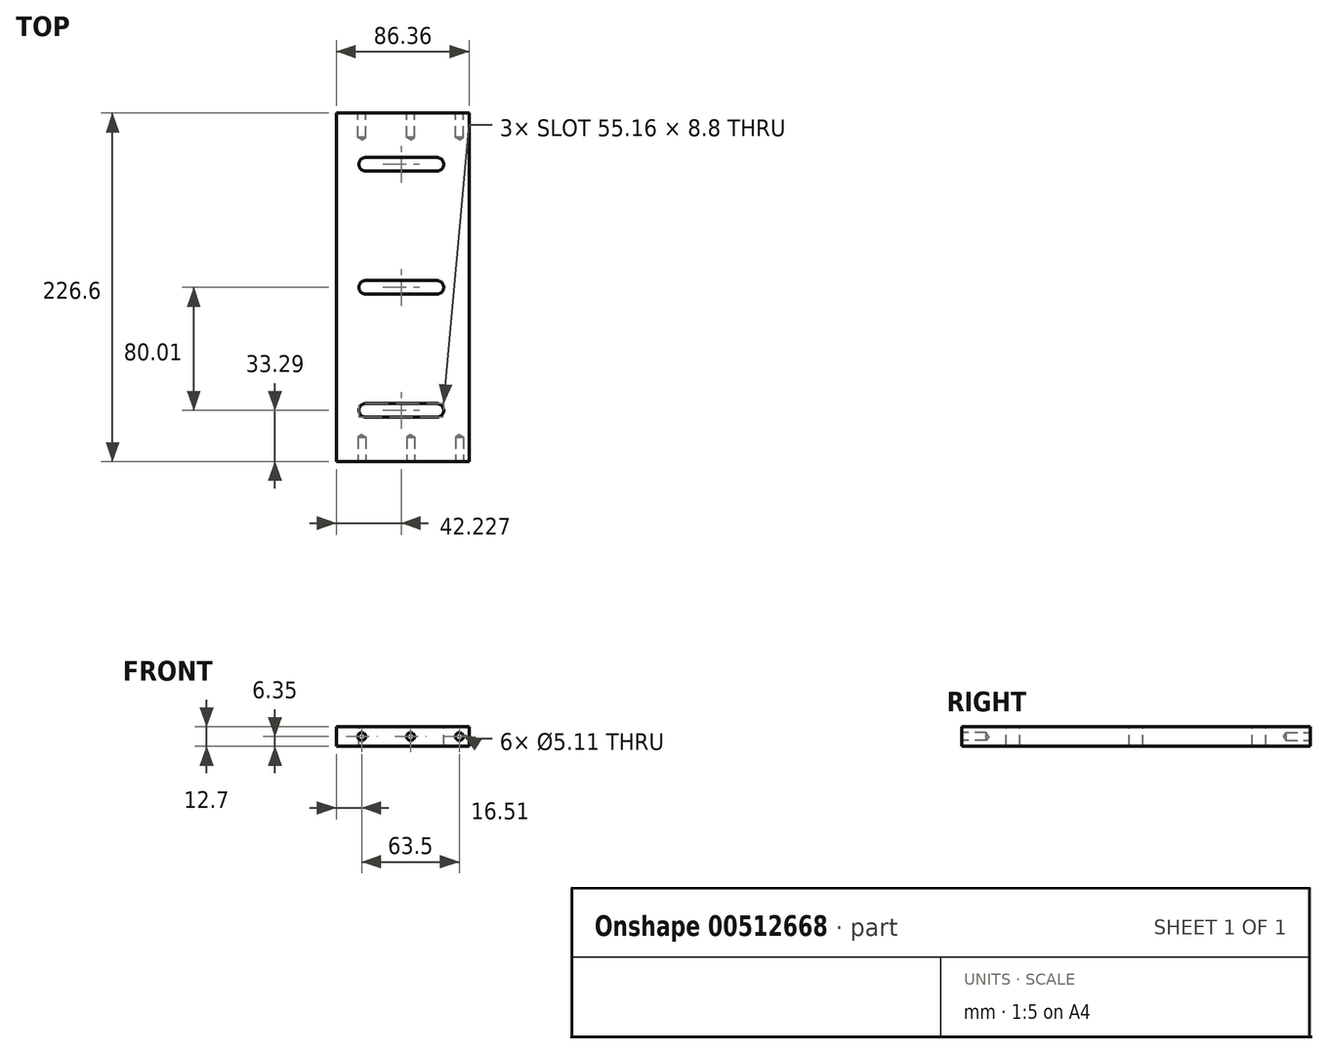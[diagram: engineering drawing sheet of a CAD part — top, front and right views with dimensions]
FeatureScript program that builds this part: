
annotation { "Feature Type Name" : "Feature", "Feature Type Description" : "" }
export const myFeature = defineFeature(function(context is Context, id is Id, definition is map)
    precondition{}
    {
        {
            var Q0;
            Q0=qCreatedBy(makeId("Front.planeOp"),FACE);
            var sketch = newSketch(context, id + "F0", { "sketchPlane" : qUnion([Q0])});
            skLineSegment(sketch, "E0.bottom", {"start": v(0, 0) * mm, "end": v(86.36, 0) * mm});
            skLineSegment(sketch, "E0.top", {"start": v(0, 12.7) * mm, "end": v(86.36, 12.7) * mm});
            skLineSegment(sketch, "E0.left", {"start": v(0, 0) * mm, "end": v(0, 12.7) * mm});
            skLineSegment(sketch, "E0.right", {"start": v(86.36, 0) * mm, "end": v(86.36, 12.7) * mm});
            skSolve(sketch);
        }
        {
            var Q0;
            Q0=makeQuery(id+"F0.imprint","IMPRINT",FACE,{"disambiguationData":[TD([[makeQuery(id+"F0.imprint","IMPRINT",EDGE,{"derivedFrom":sQuery(id+"F0.wireOp",EDGE,"E0.bottom")}),1.0]])]});
            extrude(context, id + "F1", {"entities" : qUnion([Q0]), "depth" : 252 * mm - 25.4 * mm, "offsetDistance" : 25.4 * mm});
        }
        {
            var Q0;
            Q0=makeQuery(id+"F1.opExtrude","SWEPT_FACE",FACE,{"disambiguationData":[OSD([sQuery(id+"F0.wireOp",EDGE,"E0.top")])]});
            var sketch = newSketch(context, id + "F2", { "sketchPlane" : qUnion([Q0])});
            skLineSegment(sketch, "E1", {"start": v(86.36, -226.6) * mm, "end": v(65.4, -226.6) * mm});
            skLineSegment(sketch, "E2", {"start": v(65.4, -226.6) * mm, "end": v(65.4, -193.3) * mm});
            skLineSegment(sketch, "E3", {"start": v(65.4, -193.3) * mm, "end": v(19.05, -193.3) * mm});
            skLineSegment(sketch, "E4", {"start": v(19.05, -193.3) * mm, "end": v(19.05, -113.3) * mm});
            skLineSegment(sketch, "E5", {"start": v(19.05, -113.3) * mm, "end": v(19.05, -33.29) * mm});
            skLineSegment(sketch, "E6", {"start": v(65.4, -193.3) * mm, "end": v(65.4, -113.3) * mm});
            skLineSegment(sketch, "E7", {"start": v(65.4, -113.3) * mm, "end": v(65.4, -33.29) * mm});
            skSolve(sketch);
        }
        {
            var Q0;
            Q0=sQuery(id+"F2.wireOp",VERTEX,"E5.start");
            var Q1;
            Q1=sQuery(id+"F2.wireOp",VERTEX,"E6.end");
            var Q2;
            Q2=sQuery(id+"F2.wireOp",VERTEX,"DjWuuTqk-Qcb5-qL21-kK1e-A5GOo4Qyxlcg.start");
            var Q3;
            Q3=sQuery(id+"F2.wireOp",VERTEX,"E7.end");
            var Q4;
            Q4=sQuery(id+"F2.wireOp",VERTEX,"uvlhDiYd-abZE-kXl5-hYny-CMJsfbRoTuFV.start");
            var Q5;
            Q5=sQuery(id+"F2.wireOp",VERTEX,"E4.start");
            var Q6;
            Q6=sQuery(id+"F2.wireOp",VERTEX,"E3.start");
            var Q7;
            Q7=sQuery(id+"F2.wireOp",VERTEX,"DjWuuTqk-Qcb5-qL21-kK1e-A5GOo4Qyxlcg.end");
            var Q8;
            Q8=sQuery(id+"F2.wireOp",VERTEX,"mJ9XW48N-7K4X-K1tE-wf8s-NppW8MMETJwE.end");
            var Q9;
            Q9=sQuery(id+"F2.wireOp",VERTEX,"E5.end");
            var Q10;
            Q10=makeQuery(id+"F1.opExtrude","SWEPT_BODY",BODY,{"disambiguationData":[OSD([sQuery(id+"F0.wireOp",EDGE,"E0.bottom"),sQuery(id+"F0.wireOp",EDGE,"E0.top"),sQuery(id+"F0.wireOp",EDGE,"E0.left"),sQuery(id+"F0.wireOp",EDGE,"E0.right")])]});
            hole(context, id + "F3", {"style" : HoleStyle.SIMPLE, "endStyle" : HoleEndStyle.THROUGH, "standardTappedOrClearance" : lookupTablePath({ "standard" : "ISO", "fit" : "Normal", "size" : "M8", "type" : "Clearance" }), "standardBlindInLast" : lookupTablePath({ "fit" : "Standard", "standard" : "ISO", "size" : "M8", "type" : "Clearance" }), "holeDiameter" : 8.8 * mm, "isTappedThrough" : true, "tappedDepth" : 12.7 * mm, "tapClearance" : 3, "locations" : qUnion([Q0, Q1, Q2, Q3, Q4, Q5, Q6, Q7, Q8, Q9]), "scope" : qUnion([Q10])});
        }
        {
            var Q0;
            Q0=makeQuery(id+"F1.opExtrude","SWEPT_FACE",FACE,{"disambiguationData":[OSD([sQuery(id+"F0.wireOp",EDGE,"E0.top")])]});
            var sketch = newSketch(context, id + "F4", { "sketchPlane" : qUnion([Q0])});
            skLineSegment(sketch, "E8", {"start": v(19.05, -193.3) * mm, "end": v(19.05, -197.7) * mm});
            skLineSegment(sketch, "E9", {"start": v(19.05, -197.7) * mm, "end": v(65.4, -197.7) * mm});
            skLineSegment(sketch, "E10", {"start": v(65.4, -197.7) * mm, "end": v(65.4, -188.9) * mm});
            skLineSegment(sketch, "E11", {"start": v(65.4, -188.9) * mm, "end": v(19.05, -188.9) * mm});
            skLineSegment(sketch, "E12", {"start": v(19.05, -188.9) * mm, "end": v(19.05, -193.3) * mm});
            skLineSegment(sketch, "E13.0.1.0", {"start": v(65.4, -108.9) * mm, "end": v(19.05, -108.9) * mm});
            skLineSegment(sketch, "E13.0.1.1", {"start": v(65.4, -117.7) * mm, "end": v(65.4, -108.9) * mm});
            skLineSegment(sketch, "E13.0.1.2", {"start": v(19.05, -117.7) * mm, "end": v(65.4, -117.7) * mm});
            skLineSegment(sketch, "E13.0.1.3", {"start": v(19.05, -108.9) * mm, "end": v(19.05, -113.3) * mm});
            skLineSegment(sketch, "E13.0.1.4", {"start": v(19.05, -113.3) * mm, "end": v(19.05, -117.7) * mm});
            skLineSegment(sketch, "E13.0.2.0", {"start": v(65.4, -28.89) * mm, "end": v(19.05, -28.89) * mm});
            skLineSegment(sketch, "E13.0.2.1", {"start": v(65.4, -37.69) * mm, "end": v(65.4, -28.89) * mm});
            skLineSegment(sketch, "E13.0.2.2", {"start": v(19.05, -37.69) * mm, "end": v(65.4, -37.69) * mm});
            skLineSegment(sketch, "E13.0.2.3", {"start": v(19.05, -28.89) * mm, "end": v(19.05, -33.29) * mm});
            skLineSegment(sketch, "E13.0.2.4", {"start": v(19.05, -33.29) * mm, "end": v(19.05, -37.69) * mm});
            skLineSegment(sketch, "E13.direction1", {"start": v(19.05, -197.7) * mm, "end": v(44.45, -197.7) * mm, "construction": true});
            skLineSegment(sketch, "E13.direction2", {"start": v(19.05, -197.7) * mm, "end": v(19.05, -117.7) * mm, "construction": true});
            skSolve(sketch);
        }
        {
            var Q0;
            Q0=makeQuery(id+"F1.opExtrude","CAP_FACE",FACE,{"disambiguationData":[OSD([sQuery(id+"F0.wireOp",EDGE,"E0.bottom"),sQuery(id+"F0.wireOp",EDGE,"E0.top"),sQuery(id+"F0.wireOp",EDGE,"E0.left"),sQuery(id+"F0.wireOp",EDGE,"E0.right")])],"isStart":false});
            var sketch = newSketch(context, id + "F5", { "sketchPlane" : qUnion([Q0])});
            skLineSegment(sketch, "E14", {"start": v(86.36, 6.35) * mm, "end": v(80.01, 6.35) * mm});
            skPoint(sketch, "E14.endSnap0", {"position": v(86.36, 6.35) * mm});
            skLineSegment(sketch, "E15", {"start": v(80.01, 6.35) * mm, "end": v(48.26, 6.35) * mm});
            skLineSegment(sketch, "E16", {"start": v(48.26, 6.35) * mm, "end": v(16.51, 6.35) * mm});
            skSolve(sketch);
        }
        {
            var Q0;
            Q0=sQuery(id+"F5.wireOp",VERTEX,"E16.end");
            var Q1;
            Q1=sQuery(id+"F5.wireOp",VERTEX,"E16.start");
            var Q2;
            Q2=sQuery(id+"F5.wireOp",VERTEX,"E15.start");
            var Q3;
            Q3=makeQuery(id+"F1.opExtrude","SWEPT_BODY",BODY,{"disambiguationData":[OSD([sQuery(id+"F0.wireOp",EDGE,"E0.bottom"),sQuery(id+"F0.wireOp",EDGE,"E0.top"),sQuery(id+"F0.wireOp",EDGE,"E0.left"),sQuery(id+"F0.wireOp",EDGE,"E0.right")])]});
            hole(context, id + "F6", {"style" : HoleStyle.SIMPLE, "endStyle" : HoleEndStyle.BLIND, "standardTappedOrClearance" : lookupTablePath({ "standard" : "ANSI", "engagement" : "75%", "pitch" : "20 tpi", "size" : "1/4", "type" : "Tapped" }), "standardBlindInLast" : lookupTablePath({ "standard" : "ANSI", "engagement" : "75%", "pitch" : "20 tpi", "size" : "1/4", "type" : "Tapped" }), "holeDiameter" : 5.1 * mm, "showTappedDepth" : true, "holeDepth" : 15.88 * mm, "isTappedThrough" : true, "tappedDepth" : 12.06 * mm, "tapClearance" : 3, "locations" : qUnion([Q0, Q1, Q2]), "scope" : qUnion([Q3]), "majorDiameter" : 6.35 * mm});
        }
        {
            var Q0;
            Q0=makeQuery(id+"F1.opExtrude","CAP_FACE",FACE,{"disambiguationData":[OSD([sQuery(id+"F0.wireOp",EDGE,"E0.bottom"),sQuery(id+"F0.wireOp",EDGE,"E0.top"),sQuery(id+"F0.wireOp",EDGE,"E0.left"),sQuery(id+"F0.wireOp",EDGE,"E0.right")])],"isStart":true});
            var sketch = newSketch(context, id + "F7", { "sketchPlane" : qUnion([Q0])});
            skLineSegment(sketch, "E17", {"start": v(-86.36, 6.35) * mm, "end": v(-80.01, 6.35) * mm});
            skLineSegment(sketch, "E18", {"start": v(-80.01, 6.35) * mm, "end": v(-48.26, 6.35) * mm});
            skLineSegment(sketch, "E19", {"start": v(-48.26, 6.35) * mm, "end": v(-16.51, 6.35) * mm});
            skSolve(sketch);
        }
        {
            var Q0;
            Q0=sQuery(id+"F7.wireOp",VERTEX,"E18.start");
            var Q1;
            Q1=sQuery(id+"F7.wireOp",VERTEX,"E19.start");
            var Q2;
            Q2=sQuery(id+"F7.wireOp",VERTEX,"E19.end");
            var Q3;
            Q3=makeQuery(id+"F1.opExtrude","SWEPT_BODY",BODY,{"disambiguationData":[OSD([sQuery(id+"F0.wireOp",EDGE,"E0.bottom"),sQuery(id+"F0.wireOp",EDGE,"E0.top"),sQuery(id+"F0.wireOp",EDGE,"E0.left"),sQuery(id+"F0.wireOp",EDGE,"E0.right")])]});
            hole(context, id + "F8", {"style" : HoleStyle.SIMPLE, "endStyle" : HoleEndStyle.BLIND, "standardTappedOrClearance" : lookupTablePath({ "standard" : "ANSI", "engagement" : "75%", "pitch" : "20 tpi", "size" : "1/4", "type" : "Tapped" }), "standardBlindInLast" : lookupTablePath({ "standard" : "ANSI", "engagement" : "75%", "pitch" : "20 tpi", "size" : "1/4", "type" : "Tapped" }), "holeDiameter" : 5.1 * mm, "showTappedDepth" : true, "holeDepth" : 15.88 * mm, "isTappedThrough" : true, "tappedDepth" : 12.06 * mm, "tapClearance" : 3, "locations" : qUnion([Q0, Q1, Q2]), "scope" : qUnion([Q3]), "majorDiameter" : 6.35 * mm});
        }
        {
            var Q0;
            {var subQ0=sQuery(id+"F4.wireOp",EDGE,"Ivm0cHr8-PTyv-SvoG-cq1D-oq2pNyqplCew");Q0=makeQuery(id+"F4.imprint","IMPRINT",FACE,{"disambiguationData":[TD([[makeQuery(id+"F4.imprint","IMPRINT",EDGE,{"derivedFrom":subQ0}),1.0]])]});}
            var Q1;
            {var subQ1=sQuery(id+"F4.wireOp",EDGE,"e41f544b-b3f6-454d-b319-89431cff14ae.0.1.1");Q1=makeQuery(id+"F4.imprint","IMPRINT",FACE,{"disambiguationData":[TD([[makeQuery(id+"F4.imprint","IMPRINT",EDGE,{"derivedFrom":subQ1}),1.0]])]});}
            var Q2;
            {var subQ1=sQuery(id+"F4.wireOp",EDGE,"e41f544b-b3f6-454d-b319-89431cff14ae.0.2.1");Q2=makeQuery(id+"F4.imprint","IMPRINT",FACE,{"disambiguationData":[TD([[makeQuery(id+"F4.imprint","IMPRINT",EDGE,{"derivedFrom":subQ1}),1.0]])]});}
            var Q3;
            {var subQ1=sQuery(id+"F4.wireOp",EDGE,"e41f544b-b3f6-454d-b319-89431cff14ae.0.3.1");Q3=makeQuery(id+"F4.imprint","IMPRINT",FACE,{"disambiguationData":[TD([[makeQuery(id+"F4.imprint","IMPRINT",EDGE,{"derivedFrom":subQ1}),1.0]])]});}
            var Q4;
            {var subQ0=sQuery(id+"F4.wireOp",EDGE,"E9");Q4=makeQuery(id+"F4.imprint","IMPRINT",FACE,{"disambiguationData":[TD([[makeQuery(id+"F4.imprint","IMPRINT",EDGE,{"derivedFrom":subQ0}),1.0]])]});}
            var Q5;
            {var subQ0=sQuery(id+"F4.wireOp",EDGE,"E13.0.1.0");Q5=makeQuery(id+"F4.imprint","IMPRINT",FACE,{"disambiguationData":[TD([[makeQuery(id+"F4.imprint","IMPRINT",EDGE,{"derivedFrom":subQ0}),1.0]])]});}
            var Q6;
            {var subQ0=sQuery(id+"F4.wireOp",EDGE,"E13.0.2.0");Q6=makeQuery(id+"F4.imprint","IMPRINT",FACE,{"disambiguationData":[TD([[makeQuery(id+"F4.imprint","IMPRINT",EDGE,{"derivedFrom":subQ0}),1.0]])]});}
            extrude(context, id + "F9", {"entities" : qUnion([Q0, Q1, Q2, Q3, Q4, Q5, Q6]), "operationType" : NewBodyOperationType.REMOVE, "oppositeDirection" : true, "depth" : 25.4 * mm, "offsetDistance" : 25.4 * mm});
        }
    });
